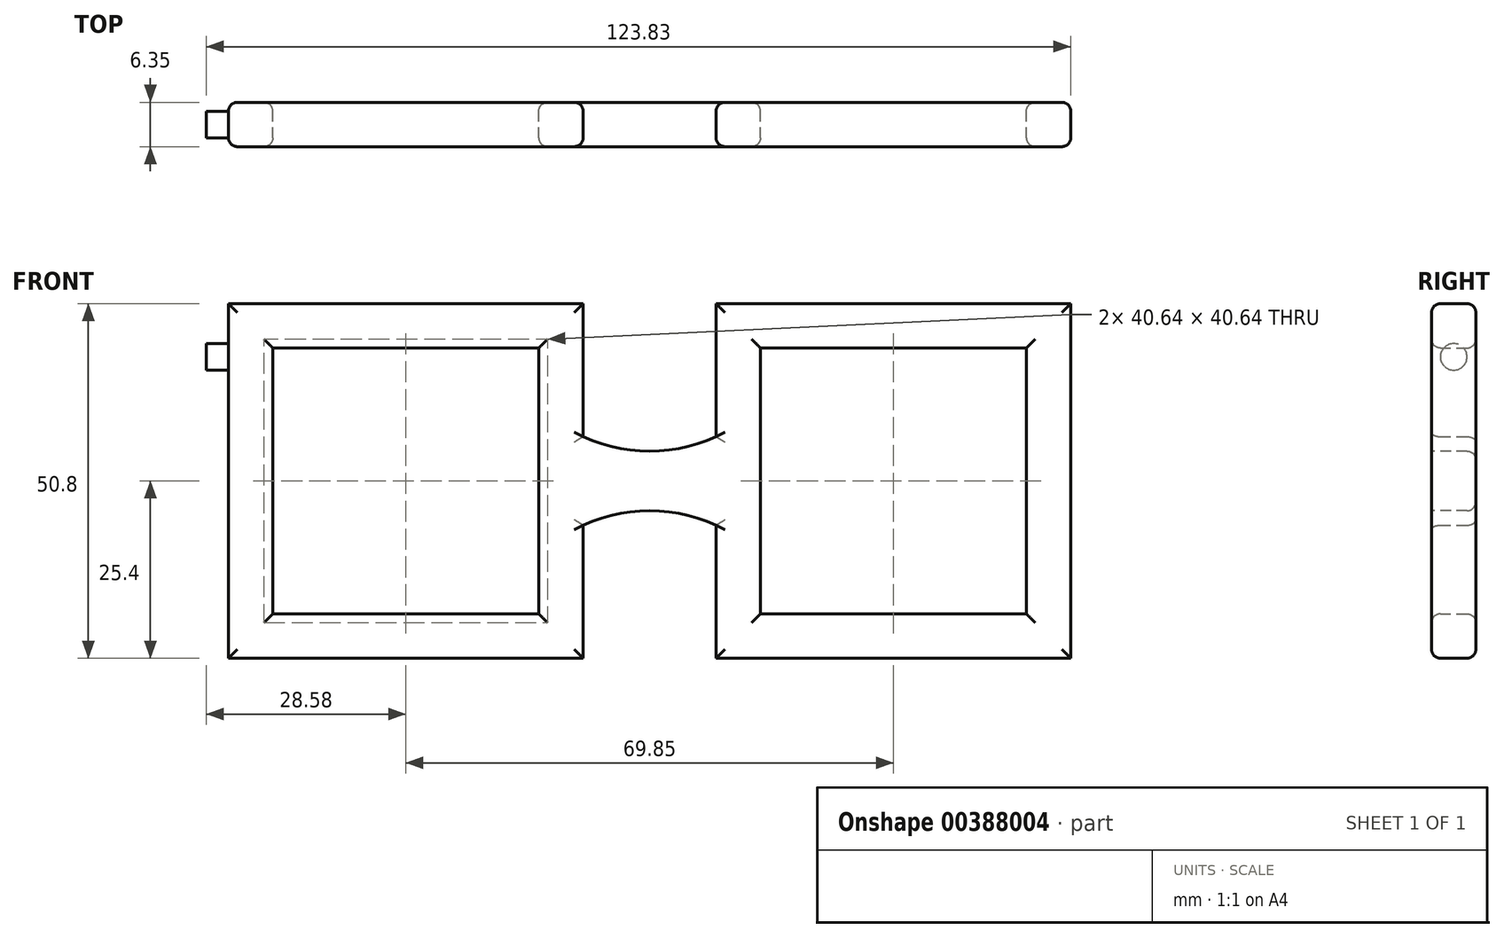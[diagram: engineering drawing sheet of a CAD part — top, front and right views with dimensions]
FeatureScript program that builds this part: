
annotation { "Feature Type Name" : "Feature", "Feature Type Description" : "" }
export const myFeature = defineFeature(function(context is Context, id is Id, definition is map)
    precondition{}
    {
        {
            var Q0;
            Q0=qCreatedBy(makeId("Front.planeOp"),FACE);
            var sketch = newSketch(context, id + "F0", { "sketchPlane" : qUnion([Q0])});
            skLineSegment(sketch, "E0", {"start": v(0, 31.75) * mm, "end": v(-50.8, 31.75) * mm});
            skLineSegment(sketch, "E1", {"start": v(-50.8, 31.75) * mm, "end": v(-50.8, -19.05) * mm});
            skLineSegment(sketch, "E2", {"start": v(-50.8, -19.05) * mm, "end": v(0, -19.05) * mm});
            skLineSegment(sketch, "E3", {"start": v(0, -19.05) * mm, "end": v(0, 0) * mm});
            skLineSegment(sketch, "E4", {"start": v(0, 0) * mm, "end": v(19.05, 0) * mm});
            skLineSegment(sketch, "E5", {"start": v(19.05, 0) * mm, "end": v(19.05, -19.05) * mm});
            skLineSegment(sketch, "E6", {"start": v(19.05, -19.05) * mm, "end": v(69.85, -19.05) * mm});
            skLineSegment(sketch, "E7", {"start": v(69.85, -19.05) * mm, "end": v(69.85, 31.75) * mm});
            skLineSegment(sketch, "E8", {"start": v(69.85, 31.75) * mm, "end": v(19.05, 31.75) * mm});
            skLineSegment(sketch, "E9", {"start": v(19.05, 31.75) * mm, "end": v(19.05, 12.7) * mm});
            skLineSegment(sketch, "E10", {"start": v(19.05, 12.7) * mm, "end": v(0, 12.7) * mm});
            skLineSegment(sketch, "E11", {"start": v(0, 12.7) * mm, "end": v(0, 31.75) * mm});
            skLineSegment(sketch, "E12.bottom", {"start": v(-44.45, 25.4) * mm, "end": v(-6.35, 25.4) * mm});
            skLineSegment(sketch, "E12.top", {"start": v(-44.45, -12.7) * mm, "end": v(-6.35, -12.7) * mm});
            skLineSegment(sketch, "E12.left", {"start": v(-44.45, 25.4) * mm, "end": v(-44.45, -12.7) * mm});
            skLineSegment(sketch, "E12.right", {"start": v(-6.35, 25.4) * mm, "end": v(-6.35, -12.7) * mm});
            skLineSegment(sketch, "E13.bottom", {"start": v(25.4, 25.4) * mm, "end": v(63.5, 25.4) * mm});
            skLineSegment(sketch, "E13.top", {"start": v(25.4, -12.7) * mm, "end": v(63.5, -12.7) * mm});
            skLineSegment(sketch, "E13.left", {"start": v(25.4, 25.4) * mm, "end": v(25.4, -12.7) * mm});
            skLineSegment(sketch, "E13.right", {"start": v(63.5, 25.4) * mm, "end": v(63.5, -12.7) * mm});
            skSolve(sketch);
        }
        {
            var Q0;
            Q0=makeQuery(id+"F0.imprint","IMPRINT",FACE,{"disambiguationData":[TD([[makeQuery(id+"F0.imprint","IMPRINT",EDGE,{"derivedFrom":sQuery(id+"F0.wireOp",EDGE,"E0")}),1.0]])]});
            extrude(context, id + "F1", {"entities" : qUnion([Q0]), "depth" : 6.35 * mm});
        }
        {
            var Q0;
            Q0=makeQuery(id+"F1.opExtrude","SWEPT_FACE",FACE,{"disambiguationData":[OSD([sQuery(id+"F0.wireOp",EDGE,"E1")])]});
            var sketch = newSketch(context, id + "F2", { "sketchPlane" : qUnion([Q0])});
            skCircle(sketch, "E14", {"center": v(3.18, 24.13) * mm, "radius": 1.9 * mm});
            skSolve(sketch);
        }
        {
            var Q0;
            Q0=makeQuery(id+"F1.opExtrude","CAP_FACE",FACE,{"disambiguationData":[OSD([sQuery(id+"F0.wireOp",EDGE,"E0"),sQuery(id+"F0.wireOp",EDGE,"E1"),sQuery(id+"F0.wireOp",EDGE,"E2"),sQuery(id+"F0.wireOp",EDGE,"E3"),sQuery(id+"F0.wireOp",EDGE,"E4"),sQuery(id+"F0.wireOp",EDGE,"E5"),sQuery(id+"F0.wireOp",EDGE,"E6"),sQuery(id+"F0.wireOp",EDGE,"E7"),sQuery(id+"F0.wireOp",EDGE,"E8"),sQuery(id+"F0.wireOp",EDGE,"E9"),sQuery(id+"F0.wireOp",EDGE,"E10"),sQuery(id+"F0.wireOp",EDGE,"E11"),sQuery(id+"F0.wireOp",EDGE,"E12.bottom"),sQuery(id+"F0.wireOp",EDGE,"E12.top"),sQuery(id+"F0.wireOp",EDGE,"E12.left"),sQuery(id+"F0.wireOp",EDGE,"E12.right"),sQuery(id+"F0.wireOp",EDGE,"E13.bottom"),sQuery(id+"F0.wireOp",EDGE,"E13.top"),sQuery(id+"F0.wireOp",EDGE,"E13.left"),sQuery(id+"F0.wireOp",EDGE,"E13.right")])],"isStart":false});
            var sketch = newSketch(context, id + "F3", { "sketchPlane" : qUnion([Q0])});
            skArc(sketch, "E15", {"start": v(19.05, 0) * mm, "mid": v(9.52, 2.08) * mm, "end": v(0, 0) * mm});
            skLineSegment(sketch, "E16", {"start": v(0, 0) * mm, "end": v(19.05, 0) * mm});
            skArc(sketch, "E17", {"start": v(0, 12.7) * mm, "mid": v(9.52, 10.62) * mm, "end": v(19.05, 12.7) * mm});
            skLineSegment(sketch, "E18", {"start": v(0, 12.7) * mm, "end": v(19.05, 12.7) * mm});
            skSolve(sketch);
        }
        {
            var Q0;
            Q0 = qSketchRegion(id + "F3", true);
            var Q1;
            {var subQ0=sQuery(id+"F3.wireOp",EDGE,"B7Htj7Yo-kReB-qe1n-0RK9-ed0PGWWS7wpv");Q1=makeQuery(id+"F3.imprint","IMPRINT",FACE,{"disambiguationData":[TD([[makeQuery(id+"F3.imprint","IMPRINT",EDGE,{"derivedFrom":subQ0}),1.0]])]});}
            extrude(context, id + "F4", {"entities" : qUnion([Q0, Q1]), "operationType" : NewBodyOperationType.ADD, "oppositeDirection" : true, "depth" : 6.35 * mm});
        }
        {
            var Q0;
            Q0 = qSketchRegion(id + "F3", true);
            extrude(context, id + "F5", {"entities" : qUnion([Q0]), "operationType" : NewBodyOperationType.REMOVE, "endBound" : BoundingType.THROUGH_ALL, "oppositeDirection" : true, "depth" : 25.4 * mm});
        }
        {
            var Q0;
            Q0=makeQuery(id+"F2.imprint","IMPRINT",FACE,{"disambiguationData":[TD([[makeQuery(id+"F2.imprint","IMPRINT",EDGE,{"derivedFrom":sQuery(id+"F2.wireOp",EDGE,"E14")}),1.0]])]});
            extrude(context, id + "F6", {"entities" : qUnion([Q0]), "operationType" : NewBodyOperationType.ADD, "endBound" : BoundingType.SYMMETRIC, "depth" : 6.35 * mm});
        }
        {
            var Q0;
            Q0=makeQuery(id+"F1.opExtrude","CAP_EDGE",EDGE,{"disambiguationData":[OSD([sQuery(id+"F0.wireOp",EDGE,"E0")])],"isStart":false});
            var Q1;
            Q1=makeQuery(id+"F1.opExtrude","CAP_EDGE",EDGE,{"disambiguationData":[OSD([sQuery(id+"F0.wireOp",EDGE,"E1")])],"isStart":false});
            var Q2;
            Q2=makeQuery(id+"F1.opExtrude","CAP_EDGE",EDGE,{"disambiguationData":[OSD([sQuery(id+"F0.wireOp",EDGE,"E2")])],"isStart":false});
            var Q3;
            Q3=makeQuery(id+"F1.opExtrude","CAP_EDGE",EDGE,{"disambiguationData":[OSD([sQuery(id+"F0.wireOp",EDGE,"E3")])],"isStart":false});
            var Q4;
            Q4=makeQuery(id+"F1.opExtrude","CAP_EDGE",EDGE,{"disambiguationData":[OSD([sQuery(id+"F0.wireOp",EDGE,"E11")])],"isStart":false});
            var Q5;
            Q5=makeQuery(id+"F1.opExtrude","CAP_EDGE",EDGE,{"disambiguationData":[OSD([sQuery(id+"F0.wireOp",EDGE,"E9")])],"isStart":false});
            var Q6;
            Q6=makeQuery(id+"F1.opExtrude","CAP_EDGE",EDGE,{"disambiguationData":[OSD([sQuery(id+"F0.wireOp",EDGE,"E5")])],"isStart":false});
            var Q7;
            Q7=makeQuery(id+"F1.opExtrude","CAP_EDGE",EDGE,{"disambiguationData":[OSD([sQuery(id+"F0.wireOp",EDGE,"E6")])],"isStart":false});
            var Q8;
            Q8=makeQuery(id+"F1.opExtrude","CAP_EDGE",EDGE,{"disambiguationData":[OSD([sQuery(id+"F0.wireOp",EDGE,"E7")])],"isStart":false});
            var Q9;
            Q9=makeQuery(id+"F1.opExtrude","CAP_EDGE",EDGE,{"disambiguationData":[OSD([sQuery(id+"F0.wireOp",EDGE,"E8")])],"isStart":false});
            var Q10;
            Q10=makeQuery(id+"F1.opExtrude","CAP_EDGE",EDGE,{"disambiguationData":[OSD([sQuery(id+"F0.wireOp",EDGE,"E8")])],"isStart":true});
            var Q11;
            Q11=makeQuery(id+"F1.opExtrude","CAP_EDGE",EDGE,{"disambiguationData":[OSD([sQuery(id+"F0.wireOp",EDGE,"E9")])],"isStart":true});
            var Q12;
            Q12=makeQuery(id+"F1.opExtrude","CAP_EDGE",EDGE,{"disambiguationData":[OSD([sQuery(id+"F0.wireOp",EDGE,"E11")])],"isStart":true});
            var Q13;
            Q13=makeQuery(id+"F1.opExtrude","CAP_EDGE",EDGE,{"disambiguationData":[OSD([sQuery(id+"F0.wireOp",EDGE,"E0")])],"isStart":true});
            var Q14;
            Q14=makeQuery(id+"F1.opExtrude","CAP_EDGE",EDGE,{"disambiguationData":[OSD([sQuery(id+"F0.wireOp",EDGE,"E1")])],"isStart":true});
            var Q15;
            Q15=makeQuery(id+"F1.opExtrude","CAP_EDGE",EDGE,{"disambiguationData":[OSD([sQuery(id+"F0.wireOp",EDGE,"E2")])],"isStart":true});
            var Q16;
            Q16=makeQuery(id+"F1.opExtrude","CAP_EDGE",EDGE,{"disambiguationData":[OSD([sQuery(id+"F0.wireOp",EDGE,"E3")])],"isStart":true});
            var Q17;
            Q17=makeQuery(id+"F1.opExtrude","CAP_EDGE",EDGE,{"disambiguationData":[OSD([sQuery(id+"F0.wireOp",EDGE,"E5")])],"isStart":true});
            var Q18;
            Q18=makeQuery(id+"F1.opExtrude","CAP_EDGE",EDGE,{"disambiguationData":[OSD([sQuery(id+"F0.wireOp",EDGE,"E6")])],"isStart":true});
            var Q19;
            Q19=makeQuery(id+"F1.opExtrude","CAP_EDGE",EDGE,{"disambiguationData":[OSD([sQuery(id+"F0.wireOp",EDGE,"E7")])],"isStart":true});
            var Q20;
            Q20=makeQuery(id+"F5.boolean.opBoolean","COPY",EDGE,{"derivedFrom":makeQuery(id+"F5.opExtrude","CAP_EDGE",EDGE,{"disambiguationData":[OSD([sQuery(id+"F3.wireOp",EDGE,"E17")])],"isStart":true})});
            var Q21;
            Q21=makeQuery(id+"F5.boolean.opBoolean","INTERSECT",EDGE,{"derivedFrom":[makeQuery(id+"F1.opExtrude","CAP_FACE",FACE,{"disambiguationData":[OSD([sQuery(id+"F0.wireOp",EDGE,"E0"),sQuery(id+"F0.wireOp",EDGE,"E1"),sQuery(id+"F0.wireOp",EDGE,"E2"),sQuery(id+"F0.wireOp",EDGE,"E3"),sQuery(id+"F0.wireOp",EDGE,"E4"),sQuery(id+"F0.wireOp",EDGE,"E5"),sQuery(id+"F0.wireOp",EDGE,"E6"),sQuery(id+"F0.wireOp",EDGE,"E7"),sQuery(id+"F0.wireOp",EDGE,"E8"),sQuery(id+"F0.wireOp",EDGE,"E9"),sQuery(id+"F0.wireOp",EDGE,"E10"),sQuery(id+"F0.wireOp",EDGE,"E11"),sQuery(id+"F0.wireOp",EDGE,"E12.bottom"),sQuery(id+"F0.wireOp",EDGE,"E12.top"),sQuery(id+"F0.wireOp",EDGE,"E12.left"),sQuery(id+"F0.wireOp",EDGE,"E12.right"),sQuery(id+"F0.wireOp",EDGE,"E13.bottom"),sQuery(id+"F0.wireOp",EDGE,"E13.top"),sQuery(id+"F0.wireOp",EDGE,"E13.left"),sQuery(id+"F0.wireOp",EDGE,"E13.right")])],"isStart":true}),makeQuery(id+"F5.opExtrude","SWEPT_FACE",FACE,{"disambiguationData":[OSD([sQuery(id+"F3.wireOp",EDGE,"E17")])]})]});
            var Q22;
            Q22=makeQuery(id+"F5.boolean.opBoolean","INTERSECT",EDGE,{"derivedFrom":[makeQuery(id+"F1.opExtrude","CAP_FACE",FACE,{"disambiguationData":[OSD([sQuery(id+"F0.wireOp",EDGE,"E0"),sQuery(id+"F0.wireOp",EDGE,"E1"),sQuery(id+"F0.wireOp",EDGE,"E2"),sQuery(id+"F0.wireOp",EDGE,"E3"),sQuery(id+"F0.wireOp",EDGE,"E4"),sQuery(id+"F0.wireOp",EDGE,"E5"),sQuery(id+"F0.wireOp",EDGE,"E6"),sQuery(id+"F0.wireOp",EDGE,"E7"),sQuery(id+"F0.wireOp",EDGE,"E8"),sQuery(id+"F0.wireOp",EDGE,"E9"),sQuery(id+"F0.wireOp",EDGE,"E10"),sQuery(id+"F0.wireOp",EDGE,"E11"),sQuery(id+"F0.wireOp",EDGE,"E12.bottom"),sQuery(id+"F0.wireOp",EDGE,"E12.top"),sQuery(id+"F0.wireOp",EDGE,"E12.left"),sQuery(id+"F0.wireOp",EDGE,"E12.right"),sQuery(id+"F0.wireOp",EDGE,"E13.bottom"),sQuery(id+"F0.wireOp",EDGE,"E13.top"),sQuery(id+"F0.wireOp",EDGE,"E13.left"),sQuery(id+"F0.wireOp",EDGE,"E13.right")])],"isStart":true}),makeQuery(id+"F5.opExtrude","SWEPT_FACE",FACE,{"disambiguationData":[OSD([sQuery(id+"F3.wireOp",EDGE,"E15")])]})]});
            var Q23;
            Q23=makeQuery(id+"F5.boolean.opBoolean","COPY",EDGE,{"derivedFrom":makeQuery(id+"F5.opExtrude","CAP_EDGE",EDGE,{"disambiguationData":[OSD([sQuery(id+"F3.wireOp",EDGE,"E15")])],"isStart":true})});
            var Q24;
            Q24=makeQuery(id+"F1.opExtrude","CAP_EDGE",EDGE,{"disambiguationData":[OSD([sQuery(id+"F0.wireOp",EDGE,"E13.left")])],"isStart":false});
            var Q25;
            Q25=makeQuery(id+"F1.opExtrude","CAP_EDGE",EDGE,{"disambiguationData":[OSD([sQuery(id+"F0.wireOp",EDGE,"E13.left")])],"isStart":true});
            var Q26;
            Q26=makeQuery(id+"F1.opExtrude","CAP_EDGE",EDGE,{"disambiguationData":[OSD([sQuery(id+"F0.wireOp",EDGE,"E13.top")])],"isStart":false});
            var Q27;
            Q27=makeQuery(id+"F1.opExtrude","CAP_EDGE",EDGE,{"disambiguationData":[OSD([sQuery(id+"F0.wireOp",EDGE,"E13.top")])],"isStart":true});
            var Q28;
            Q28=makeQuery(id+"F1.opExtrude","CAP_EDGE",EDGE,{"disambiguationData":[OSD([sQuery(id+"F0.wireOp",EDGE,"E13.right")])],"isStart":false});
            var Q29;
            Q29=makeQuery(id+"F1.opExtrude","CAP_EDGE",EDGE,{"disambiguationData":[OSD([sQuery(id+"F0.wireOp",EDGE,"E13.right")])],"isStart":true});
            var Q30;
            Q30=makeQuery(id+"F1.opExtrude","CAP_EDGE",EDGE,{"disambiguationData":[OSD([sQuery(id+"F0.wireOp",EDGE,"E13.bottom")])],"isStart":true});
            var Q31;
            Q31=makeQuery(id+"F1.opExtrude","CAP_EDGE",EDGE,{"disambiguationData":[OSD([sQuery(id+"F0.wireOp",EDGE,"E13.bottom")])],"isStart":false});
            var Q32;
            Q32=makeQuery(id+"F1.opExtrude","CAP_EDGE",EDGE,{"disambiguationData":[OSD([sQuery(id+"F0.wireOp",EDGE,"E12.bottom")])],"isStart":false});
            var Q33;
            Q33=makeQuery(id+"F1.opExtrude","CAP_EDGE",EDGE,{"disambiguationData":[OSD([sQuery(id+"F0.wireOp",EDGE,"E12.bottom")])],"isStart":true});
            var Q34;
            Q34=makeQuery(id+"F1.opExtrude","CAP_EDGE",EDGE,{"disambiguationData":[OSD([sQuery(id+"F0.wireOp",EDGE,"E12.left")])],"isStart":true});
            var Q35;
            Q35=makeQuery(id+"F1.opExtrude","CAP_EDGE",EDGE,{"disambiguationData":[OSD([sQuery(id+"F0.wireOp",EDGE,"E12.left")])],"isStart":false});
            var Q36;
            Q36=makeQuery(id+"F1.opExtrude","CAP_EDGE",EDGE,{"disambiguationData":[OSD([sQuery(id+"F0.wireOp",EDGE,"E12.top")])],"isStart":true});
            var Q37;
            Q37=makeQuery(id+"F1.opExtrude","CAP_EDGE",EDGE,{"disambiguationData":[OSD([sQuery(id+"F0.wireOp",EDGE,"E12.top")])],"isStart":false});
            var Q38;
            Q38=makeQuery(id+"F1.opExtrude","CAP_EDGE",EDGE,{"disambiguationData":[OSD([sQuery(id+"F0.wireOp",EDGE,"E12.right")])],"isStart":true});
            var Q39;
            Q39=makeQuery(id+"F1.opExtrude","CAP_EDGE",EDGE,{"disambiguationData":[OSD([sQuery(id+"F0.wireOp",EDGE,"E12.right")])],"isStart":false});
            fillet(context, id + "F7", {"entities" : qUnion([Q0, Q1, Q2, Q3, Q4, Q5, Q6, Q7, Q8, Q9, Q10, Q11, Q12, Q13, Q14, Q15, Q16, Q17, Q18, Q19, Q20, Q21, Q22, Q23, Q24, Q25, Q26, Q27, Q28, Q29, Q30, Q31, Q32, Q33, Q34, Q35, Q36, Q37, Q38, Q39]), "radius" : 1.27 * mm, "tangentPropagation" : true, "allowEdgeOverflow" : false});
        }
    });
